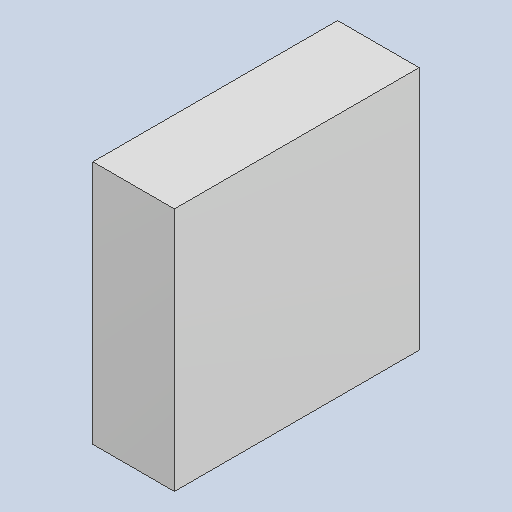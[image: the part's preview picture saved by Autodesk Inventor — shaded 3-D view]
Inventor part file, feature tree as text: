
AUTODESK INVENTOR PART (.ipt)
format: ipt  version: 2023.4 (Build 274418000, 418)  size: 81,408 bytes
history: native  units: mm
features: extrude x1
ambient origin geometry x8: Origin, YZ Plane, XZ Plane, XY Plane, X Axis, Y Axis, Z Axis, Center Point
bodies: Solid1 (feature_tree)
feature tree (1):
  extrude  "Extruded_2"  [1 undecoded]
note: 1 required parameter value undecoded (feature->parameter linkage not recoverable at this tier; creation-order binding heuristic only, values carry confidence <= 0.55)
